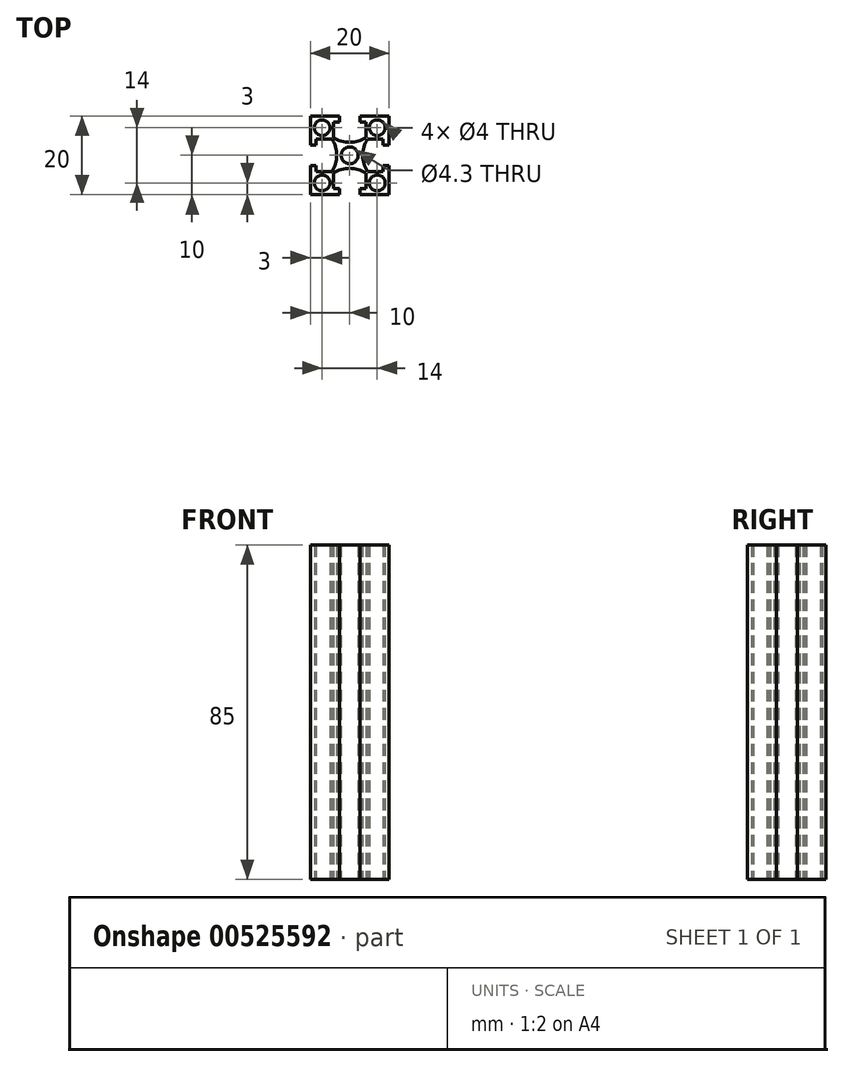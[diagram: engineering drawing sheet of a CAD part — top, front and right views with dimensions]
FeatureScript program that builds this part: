
annotation { "Feature Type Name" : "Feature", "Feature Type Description" : "" }
export const myFeature = defineFeature(function(context is Context, id is Id, definition is map)
    precondition{}
    {
        {
            var Q0;
            Q0=qCreatedBy(makeId("Top.planeOp"),FACE);
            var sketch = newSketch(context, id + "F0", { "sketchPlane" : qUnion([Q0])});
            skCircle(sketch, "E0", {"center": v(-7, 7) * mm, "radius": 2 * mm});
            skCircle(sketch, "E1.MirrorC", {"center": v(-7, -7) * mm, "radius": 2 * mm});
            skLineSegment(sketch, "E2.top", {"start": v(-10, 2.65) * mm, "end": v(-10, -2.65) * mm});
            skLineSegment(sketch, "E2.left", {"start": v(-8.5, 2.65) * mm, "end": v(-10, 2.65) * mm});
            skLineSegment(sketch, "E2.right", {"start": v(-8.5, -2.65) * mm, "end": v(-10, -2.65) * mm});
            skLineSegment(sketch, "E3.bottom", {"start": v(-8.5, 4.15) * mm, "end": v(-8.5, 2.65) * mm});
            skLineSegment(sketch, "E3.left", {"start": v(-8.5, 4.15) * mm, "end": v(-4.55, 4.15) * mm});
            skLineSegment(sketch, "E3.right", {"start": v(-8.5, -4.15) * mm, "end": v(-4.55, -4.15) * mm});
            skArc(sketch, "E4", {"start": v(-4.55, -4.15) * mm, "mid": v(-3.3, 0) * mm, "end": v(-4.55, 4.15) * mm});
            skLineSegment(sketch, "E5.trimOffspring", {"start": v(-8.5, -2.65) * mm, "end": v(-8.5, -4.15) * mm});
            skLineSegment(sketch, "E6.bottom", {"start": v(10, -10) * mm, "end": v(-10, -10) * mm});
            skLineSegment(sketch, "E6.top", {"start": v(10, 10) * mm, "end": v(-10, 10) * mm});
            skLineSegment(sketch, "E6.left", {"start": v(10, -10) * mm, "end": v(10, 10) * mm});
            skLineSegment(sketch, "E6.right", {"start": v(-10, -10) * mm, "end": v(-10, 10) * mm});
            skPoint(sketch, "E6.middle", {"position": v(0, 0) * mm});
            skCircle(sketch, "E7.MirrorC", {"center": v(7, 7) * mm, "radius": 2 * mm});
            skCircle(sketch, "E8.MirrorC", {"center": v(7, -7) * mm, "radius": 2 * mm});
            skLineSegment(sketch, "E9.1.0", {"start": v(-4.15, -8.5) * mm, "end": v(-2.65, -8.5) * mm});
            skArc(sketch, "E9.1.1", {"start": v(4.15, -4.55) * mm, "mid": v(0, -3.3) * mm, "end": v(-4.15, -4.55) * mm});
            skLineSegment(sketch, "E9.1.2", {"start": v(-2.65, -10) * mm, "end": v(2.65, -10) * mm});
            skLineSegment(sketch, "E9.1.3", {"start": v(-2.65, -8.5) * mm, "end": v(-2.65, -10) * mm});
            skLineSegment(sketch, "E9.1.4", {"start": v(-4.15, -8.5) * mm, "end": v(-4.15, -4.55) * mm});
            skLineSegment(sketch, "E9.1.5", {"start": v(2.65, -8.5) * mm, "end": v(4.15, -8.5) * mm});
            skLineSegment(sketch, "E9.1.6", {"start": v(4.15, -8.5) * mm, "end": v(4.15, -4.55) * mm});
            skLineSegment(sketch, "E9.1.7", {"start": v(2.65, -8.5) * mm, "end": v(2.65, -10) * mm});
            skLineSegment(sketch, "E9.2.0", {"start": v(8.5, -4.15) * mm, "end": v(8.5, -2.65) * mm});
            skArc(sketch, "E9.2.1", {"start": v(4.55, 4.15) * mm, "mid": v(3.3, 0) * mm, "end": v(4.55, -4.15) * mm});
            skLineSegment(sketch, "E9.2.2", {"start": v(10, -2.65) * mm, "end": v(10, 2.65) * mm});
            skLineSegment(sketch, "E9.2.3", {"start": v(8.5, -2.65) * mm, "end": v(10, -2.65) * mm});
            skLineSegment(sketch, "E9.2.4", {"start": v(8.5, -4.15) * mm, "end": v(4.55, -4.15) * mm});
            skLineSegment(sketch, "E9.2.5", {"start": v(8.5, 2.65) * mm, "end": v(8.5, 4.15) * mm});
            skLineSegment(sketch, "E9.2.6", {"start": v(8.5, 4.15) * mm, "end": v(4.55, 4.15) * mm});
            skLineSegment(sketch, "E9.2.7", {"start": v(8.5, 2.65) * mm, "end": v(10, 2.65) * mm});
            skLineSegment(sketch, "E9.3.0", {"start": v(4.15, 8.5) * mm, "end": v(2.65, 8.5) * mm});
            skArc(sketch, "E9.3.1", {"start": v(-4.15, 4.55) * mm, "mid": v(0, 3.3) * mm, "end": v(4.15, 4.55) * mm});
            skLineSegment(sketch, "E9.3.2", {"start": v(2.65, 10) * mm, "end": v(-2.65, 10) * mm});
            skLineSegment(sketch, "E9.3.3", {"start": v(2.65, 8.5) * mm, "end": v(2.65, 10) * mm});
            skLineSegment(sketch, "E9.3.4", {"start": v(4.15, 8.5) * mm, "end": v(4.15, 4.55) * mm});
            skLineSegment(sketch, "E9.3.5", {"start": v(-2.65, 8.5) * mm, "end": v(-4.15, 8.5) * mm});
            skLineSegment(sketch, "E9.3.6", {"start": v(-4.15, 8.5) * mm, "end": v(-4.15, 4.55) * mm});
            skLineSegment(sketch, "E9.3.7", {"start": v(-2.65, 8.5) * mm, "end": v(-2.65, 10) * mm});
            skCircle(sketch, "E10", {"center": v(0, 0) * mm, "radius": 2.15 * mm});
            skSolve(sketch);
        }
        {
            var Q0;
            Q0=makeQuery(id+"F0.imprint","IMPRINT",FACE,{"disambiguationData":[TD([[makeQuery(id+"F0.imprint","IMPRINT",EDGE,{"derivedFrom":sQuery(id+"F0.wireOp",EDGE,"E0")}),-1.0]])]});
            extrude(context, id + "F1", {"entities" : qUnion([Q0]), "depth" : 85 * mm, "offsetDistance" : 25 * mm});
        }
    });
